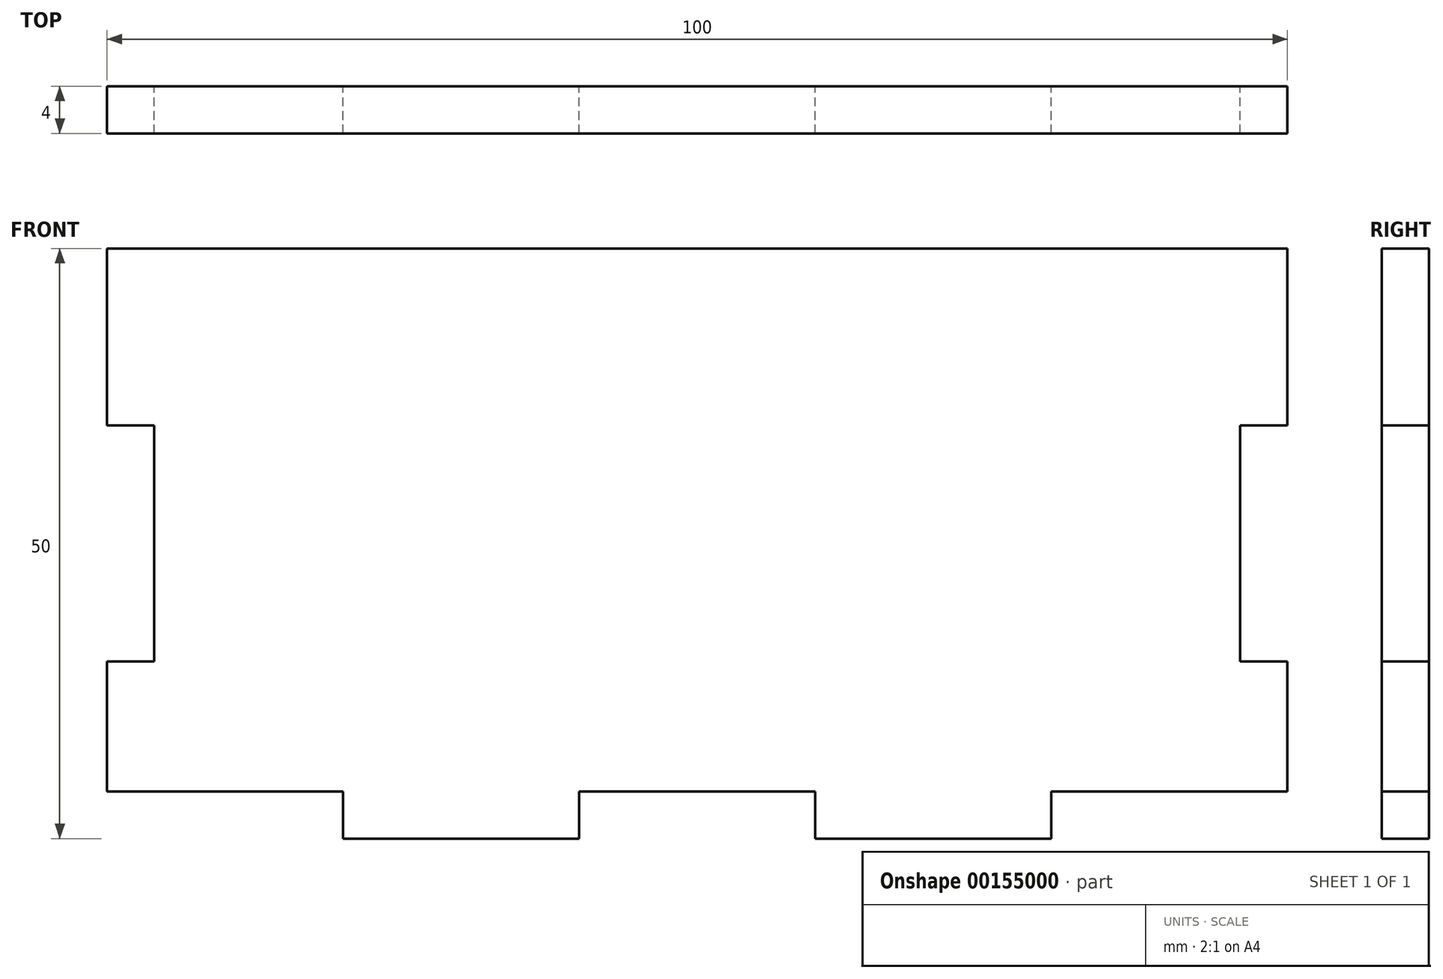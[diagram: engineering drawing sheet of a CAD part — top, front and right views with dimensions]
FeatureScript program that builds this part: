
annotation { "Feature Type Name" : "Feature", "Feature Type Description" : "" }
export const myFeature = defineFeature(function(context is Context, id is Id, definition is map)
    precondition{}
    {
        {
            var Q0;
            Q0=qCreatedBy(makeId("Front.planeOp"),FACE);
            var sketch = newSketch(context, id + "F0", { "sketchPlane" : qUnion([Q0])});
            skLineSegment(sketch, "E0.bottom", {"start": v(0, 50) * mm, "end": v(100, 50) * mm});
            skLineSegment(sketch, "E0.top", {"start": v(0, 0) * mm, "end": v(100, 0) * mm});
            skLineSegment(sketch, "E0.left", {"start": v(0, 50) * mm, "end": v(0, 0) * mm});
            skLineSegment(sketch, "E0.right", {"start": v(100, 50) * mm, "end": v(100, 0) * mm});
            skLineSegment(sketch, "E1.top", {"start": v(20, 0) * mm, "end": v(40, 0) * mm});
            skLineSegment(sketch, "E1.left", {"start": v(20, 4) * mm, "end": v(20, 0) * mm});
            skLineSegment(sketch, "E1.right", {"start": v(40, 4) * mm, "end": v(40, 0) * mm});
            skLineSegment(sketch, "E2.top", {"start": v(60, 0) * mm, "end": v(80, 0) * mm});
            skLineSegment(sketch, "E2.left", {"start": v(60, 4) * mm, "end": v(60, 0) * mm});
            skLineSegment(sketch, "E2.right", {"start": v(80, 4) * mm, "end": v(80, 0) * mm});
            skLineSegment(sketch, "E3.bottom", {"start": v(96, 35) * mm, "end": v(100, 35) * mm});
            skLineSegment(sketch, "E3.top", {"start": v(96, 15) * mm, "end": v(100, 15) * mm});
            skLineSegment(sketch, "E3.left", {"start": v(96, 35) * mm, "end": v(96, 15) * mm});
            skLineSegment(sketch, "E3.right", {"start": v(100, 35) * mm, "end": v(100, 15) * mm});
            skPoint(sketch, "E4.oppositeSnap0", {"position": v(0, 25) * mm});
            skLineSegment(sketch, "E4.bottom", {"start": v(4, 35) * mm, "end": v(0, 35) * mm});
            skLineSegment(sketch, "E4.top", {"start": v(4, 15) * mm, "end": v(0, 15) * mm});
            skLineSegment(sketch, "E4.left", {"start": v(4, 35) * mm, "end": v(4, 15) * mm});
            skLineSegment(sketch, "E4.right", {"start": v(0, 35) * mm, "end": v(0, 15) * mm});
            skLineSegment(sketch, "E5.bottom", {"start": v(20, 4) * mm, "end": v(0, 4) * mm});
            skLineSegment(sketch, "E5.top", {"start": v(20, 0) * mm, "end": v(0, 0) * mm});
            skLineSegment(sketch, "E5.right", {"start": v(0, 4) * mm, "end": v(0, 0) * mm});
            skLineSegment(sketch, "E6.bottom", {"start": v(60, 4) * mm, "end": v(40, 4) * mm});
            skLineSegment(sketch, "E6.top", {"start": v(60, 0) * mm, "end": v(40, 0) * mm});
            skLineSegment(sketch, "E7.bottom", {"start": v(80, 4) * mm, "end": v(100, 4) * mm});
            skLineSegment(sketch, "E7.top", {"start": v(80, 0) * mm, "end": v(100, 0) * mm});
            skLineSegment(sketch, "E7.right", {"start": v(100, 4) * mm, "end": v(100, 0) * mm});
            skSolve(sketch);
        }
        {
            var Q0;
            {var subQ5=sQuery(id+"F0.wireOp",EDGE,"E0.bottom");Q0=makeQuery(id+"F0.imprint","IMPRINT",FACE,{"disambiguationData":[TD([[makeQuery(id+"F0.imprint","IMPRINT",EDGE,{"derivedFrom":subQ5}),-1.0]])]});}
            extrude(context, id + "F1", {"entities" : qUnion([Q0]), "depth" : 4 * mm});
        }
    });
